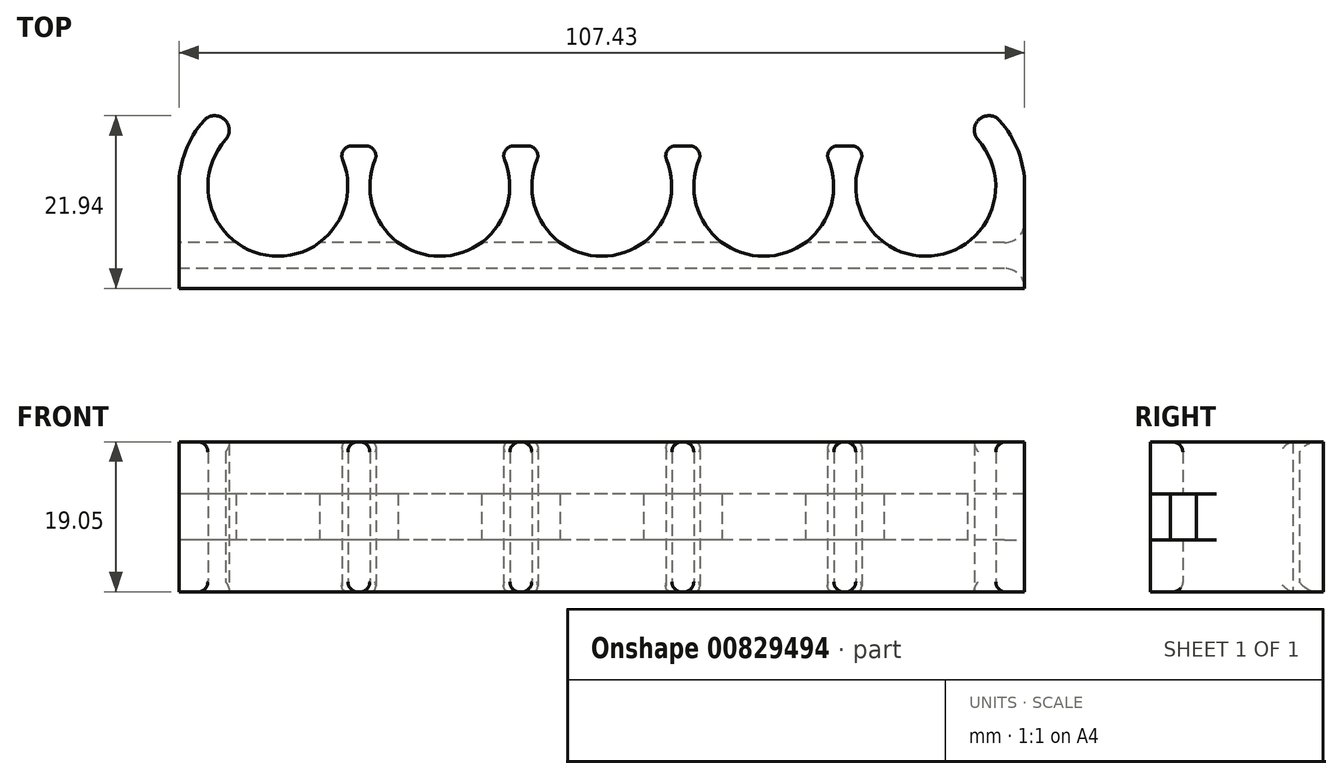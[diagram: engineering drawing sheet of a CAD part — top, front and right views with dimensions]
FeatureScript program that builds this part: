
annotation { "Feature Type Name" : "Feature", "Feature Type Description" : "" }
export const myFeature = defineFeature(function(context is Context, id is Id, definition is map)
    precondition{}
    {
        {
            var Q0;
            Q0=qCreatedBy(makeId("Top.planeOp"),FACE);
            var sketch = newSketch(context, id + "F0", { "sketchPlane" : qUnion([Q0])});
            skLineSegment(sketch, "E0.direction1", {"start": v(0, 0) * mm, "end": v(20.57, 0) * mm, "construction": true});
            skLineSegment(sketch, "E1", {"start": v(9.4, 5.14) * mm, "end": v(11.18, 5.14) * mm});
            skLineSegment(sketch, "E2", {"start": v(29.97, 5.14) * mm, "end": v(31.75, 5.14) * mm});
            skArc(sketch, "E3.MirrorCS", {"start": v(-9.4, 8.35) * mm, "mid": v(-6.78, 8.5) * mm, "end": v(-6.66, 5.9) * mm});
            skArc(sketch, "E4.MirrorCS", {"start": v(-12.57, 0) * mm, "mid": v(-11.75, 4.47) * mm, "end": v(-9.4, 8.35) * mm});
            skLineSegment(sketch, "E5.MirrorCS", {"start": v(-12.57, -12.97) * mm, "end": v(-12.57, 0) * mm});
            skArc(sketch, "E6", {"start": v(8.22, 3.38) * mm, "mid": v(-1.5, -8.76) * mm, "end": v(-6.63, 5.93) * mm});
            skArc(sketch, "E7", {"start": v(28.8, 3.38) * mm, "mid": v(20.57, -8.89) * mm, "end": v(12.35, 3.38) * mm});
            skPoint(sketch, "E8.visualSharp", {"position": v(7.26, 5.14) * mm});
            skArc(sketch, "E8.filletArc", {"start": v(9.4, 5.14) * mm, "mid": v(8.34, 4.57) * mm, "end": v(8.22, 3.38) * mm});
            skPoint(sketch, "E9.visualSharp", {"position": v(13.32, 5.14) * mm});
            skArc(sketch, "E9.filletArc", {"start": v(12.35, 3.38) * mm, "mid": v(12.23, 4.57) * mm, "end": v(11.18, 5.14) * mm});
            skPoint(sketch, "E10.visualSharp", {"position": v(27.83, 5.14) * mm});
            skArc(sketch, "E10.filletArc", {"start": v(29.97, 5.14) * mm, "mid": v(28.91, 4.57) * mm, "end": v(28.8, 3.38) * mm});
            skPoint(sketch, "E11.visualSharp", {"position": v(33.9, 5.14) * mm});
            skArc(sketch, "E11.filletArc", {"start": v(32.93, 3.38) * mm, "mid": v(32.8, 4.57) * mm, "end": v(31.75, 5.14) * mm});
            skLineSegment(sketch, "E12", {"start": v(50.54, 5.14) * mm, "end": v(52.33, 5.14) * mm});
            skArc(sketch, "E13", {"start": v(49.37, 3.38) * mm, "mid": v(41.15, -8.9) * mm, "end": v(32.93, 3.38) * mm});
            skPoint(sketch, "E14.visualSharp", {"position": v(48.4, 5.14) * mm});
            skArc(sketch, "E14.filletArc", {"start": v(50.54, 5.14) * mm, "mid": v(49.49, 4.57) * mm, "end": v(49.37, 3.38) * mm});
            skPoint(sketch, "E15.visualSharp", {"position": v(54.47, 5.14) * mm});
            skArc(sketch, "E15.filletArc", {"start": v(53.5, 3.38) * mm, "mid": v(53.38, 4.57) * mm, "end": v(52.33, 5.14) * mm});
            skLineSegment(sketch, "E16", {"start": v(94.86, -12.97) * mm, "end": v(94.86, 0) * mm});
            skLineSegment(sketch, "E17", {"start": v(71.12, 5.14) * mm, "end": v(72.9, 5.14) * mm});
            skArc(sketch, "E18", {"start": v(94.86, 0) * mm, "mid": v(94.04, 4.47) * mm, "end": v(91.69, 8.35) * mm});
            skArc(sketch, "E19", {"start": v(91.69, 8.35) * mm, "mid": v(89.09, 8.5) * mm, "end": v(88.94, 5.9) * mm});
            skArc(sketch, "E20", {"start": v(69.94, 3.38) * mm, "mid": v(61.72, -8.9) * mm, "end": v(53.5, 3.38) * mm});
            skArc(sketch, "E21", {"start": v(88.94, 5.9) * mm, "mid": v(83.79, -8.76) * mm, "end": v(74.07, 3.38) * mm});
            skPoint(sketch, "E22.visualSharp", {"position": v(68.98, 5.14) * mm});
            skArc(sketch, "E22.filletArc", {"start": v(71.12, 5.14) * mm, "mid": v(70.06, 4.57) * mm, "end": v(69.94, 3.38) * mm});
            skPoint(sketch, "E23.visualSharp", {"position": v(75.04, 5.14) * mm});
            skArc(sketch, "E23.filletArc", {"start": v(74.07, 3.38) * mm, "mid": v(73.96, 4.57) * mm, "end": v(72.9, 5.14) * mm});
            skLineSegment(sketch, "E24", {"start": v(-12.57, -12.97) * mm, "end": v(94.86, -12.97) * mm});
            skSolve(sketch);
        }
        {
            var Q0;
            Q0=makeQuery(id+"F0.imprint","IMPRINT",FACE,{"disambiguationData":[TD([[makeQuery(id+"F0.imprint","IMPRINT",EDGE,{"derivedFrom":sQuery(id+"F0.wireOp",EDGE,"E1")}),-1.0]])]});
            var Q1;
            Q1=sQuery(id+"F0.wireOp",EDGE,"369ZI1eD-I4s6-VPlC-i9KF-M6xCAj87r0oj");
            var Q2;
            Q2=sQuery(id+"F0.wireOp",EDGE,"E6");
            var Q3;
            Q3=sQuery(id+"F0.wireOp",EDGE,"E3.MirrorCS");
            var Q4;
            Q4=sQuery(id+"F0.wireOp",EDGE,"E4.MirrorCS");
            var Q5;
            Q5=sQuery(id+"F0.wireOp",EDGE,"E5.MirrorCS");
            var Q6;
            Q6=sQuery(id+"F0.wireOp",EDGE,"E7");
            var Q7;
            Q7=sQuery(id+"F0.wireOp",EDGE,"E13");
            var Q8;
            Q8=sQuery(id+"F0.wireOp",EDGE,"21338633-60fe-4fad-beaa-767240a8ec89");
            var Q9;
            Q9=sQuery(id+"F0.wireOp",EDGE,"4f3b21b5-788c-469e-a292-998afeaadf8e");
            var Q10;
            Q10=sQuery(id+"F0.wireOp",EDGE,"75842ce1-2111-4564-b153-1218a2f22df0");
            var Q11;
            Q11=sQuery(id+"F0.wireOp",EDGE,"88b2d735-7f10-4ffd-a21d-1716e4e02eba");
            var Q12;
            Q12=sQuery(id+"F0.wireOp",EDGE,"E15.filletArc");
            var Q13;
            Q13=sQuery(id+"F0.wireOp",EDGE,"E12");
            var Q14;
            Q14=sQuery(id+"F0.wireOp",EDGE,"E14.filletArc");
            var Q15;
            Q15=sQuery(id+"F0.wireOp",EDGE,"E11.filletArc");
            var Q16;
            Q16=sQuery(id+"F0.wireOp",EDGE,"E2");
            var Q17;
            Q17=sQuery(id+"F0.wireOp",EDGE,"E10.filletArc");
            var Q18;
            Q18=sQuery(id+"F0.wireOp",EDGE,"E9.filletArc");
            var Q19;
            Q19=sQuery(id+"F0.wireOp",EDGE,"E1");
            var Q20;
            Q20=sQuery(id+"F0.wireOp",EDGE,"E8.filletArc");
            extrude(context, id + "F1", {"entities" : qUnion([Q0]), "surfaceEntities" : qUnion([Q1, Q2, Q3, Q4, Q5, Q6, Q7, Q8, Q9, Q10, Q11, Q12, Q13, Q14, Q15, Q16, Q17, Q18, Q19, Q20]), "depth" : 19.05 * mm, "offsetDistance" : 25.4 * mm});
        }
        {
            var Q0;
            Q0=makeQuery(id+"F1.opExtrude","SWEPT_FACE",FACE,{"disambiguationData":[OSD([sQuery(id+"F0.wireOp",EDGE,"E5.MirrorCS")])]});
            var Q1;
            Q1 = qBodyType(qCreatedBy(id + "F3" ,EDGE), BodyType.WIRE);
            cPlane(context, id + "F2", {"entities" : qUnion([Q0, Q1]), "cplaneType" : CPlaneType.OFFSET, "offset" : 0 * mm, "width" : 152.4 * mm, "height" : 152.4 * mm});
        }
        {
            var Q0;
            Q0=qCreatedBy(id+"F2.planeOp",FACE);
            var sketch = newSketch(context, id + "F3", { "sketchPlane" : qUnion([Q0])});
            skLineSegment(sketch, "E25.bottom", {"start": v(7.13, 12.45) * mm, "end": v(10.43, 12.45) * mm});
            skLineSegment(sketch, "E25.top", {"start": v(7.13, 6.6) * mm, "end": v(10.43, 6.6) * mm});
            skLineSegment(sketch, "E25.left", {"start": v(7.13, 12.45) * mm, "end": v(7.13, 6.6) * mm});
            skLineSegment(sketch, "E25.right", {"start": v(10.43, 12.45) * mm, "end": v(10.43, 6.6) * mm});
            skLineSegment(sketch, "E26", {"start": v(10.43, 9.53) * mm, "end": v(7.13, 9.53) * mm, "construction": true});
            skLineSegment(sketch, "E27", {"start": v(12.97, 9.53) * mm, "end": v(7.13, 9.53) * mm, "construction": true});
            skSolve(sketch);
        }
        {
            var Q0;
            Q0=makeQuery(id+"F3.imprint","IMPRINT",FACE,{"disambiguationData":[TD([[makeQuery(id+"F3.imprint","IMPRINT",EDGE,{"derivedFrom":sQuery(id+"F3.wireOp",EDGE,"E25.bottom")}),-1.0]])]});
            extrude(context, id + "F4", {"entities" : qUnion([Q0]), "operationType" : NewBodyOperationType.REMOVE, "endBound" : BoundingType.THROUGH_ALL, "oppositeDirection" : true, "depth" : 25.4 * mm, "offsetDistance" : 25.4 * mm});
        }
        {
            var Q0;
            Q0=makeQuery(id+"F4.boolean.opBoolean","INTERSECT",EDGE,{"derivedFrom":[makeQuery(id+"F1.opExtrude","SWEPT_FACE",FACE,{"disambiguationData":[OSD([sQuery(id+"F0.wireOp",EDGE,"E16")])]}),makeQuery(id+"F4.opExtrude","SWEPT_FACE",FACE,{"disambiguationData":[OSD([sQuery(id+"F3.wireOp",EDGE,"E25.left")])]})]});
            var Q1;
            Q1=makeQuery(id+"F4.boolean.opBoolean","INTERSECT",EDGE,{"derivedFrom":[makeQuery(id+"F1.opExtrude","SWEPT_FACE",FACE,{"disambiguationData":[OSD([sQuery(id+"F0.wireOp",EDGE,"E16")])]}),makeQuery(id+"F4.opExtrude","SWEPT_FACE",FACE,{"disambiguationData":[OSD([sQuery(id+"F3.wireOp",EDGE,"E25.right")])]})]});
            var Q2;
            Q2=makeQuery(id+"F4.boolean.opBoolean","COPY",EDGE,{"derivedFrom":makeQuery(id+"F4.opExtrude","CAP_EDGE",EDGE,{"disambiguationData":[OSD([sQuery(id+"F3.wireOp",EDGE,"E25.left")])],"isStart":true})});
            var Q3;
            Q3=makeQuery(id+"F4.boolean.opBoolean","COPY",EDGE,{"derivedFrom":makeQuery(id+"F4.opExtrude","CAP_EDGE",EDGE,{"disambiguationData":[OSD([sQuery(id+"F3.wireOp",EDGE,"E25.right")])],"isStart":true})});
            fillet(context, id + "F5", {"entities" : qUnion([Q0, Q1, Q2, Q3]), "radius" : 2.54 * mm, "tangentPropagation" : true, "allowEdgeOverflow" : false});
        }
        {
            var Q0;
            Q0=makeQuery(id+"F1.opExtrude","CAP_EDGE",EDGE,{"disambiguationData":[OSD([sQuery(id+"F0.wireOp",EDGE,"wjlftGJZ-UNCk-L4i5-wpio-xcS1ndEBSDBN")])],"isStart":true});
            var Q1;
            Q1=makeQuery(id+"F1.opExtrude","CAP_EDGE",EDGE,{"disambiguationData":[OSD([sQuery(id+"F0.wireOp",EDGE,"E7")])],"isStart":true});
            var Q2;
            Q2=makeQuery(id+"F1.opExtrude","CAP_EDGE",EDGE,{"disambiguationData":[OSD([sQuery(id+"F0.wireOp",EDGE,"E6")])],"isStart":true});
            var Q3;
            Q3=makeQuery(id+"F1.opExtrude","CAP_EDGE",EDGE,{"disambiguationData":[OSD([sQuery(id+"F0.wireOp",EDGE,"E13")])],"isStart":true});
            var Q4;
            Q4=makeQuery(id+"F1.opExtrude","CAP_EDGE",EDGE,{"disambiguationData":[OSD([sQuery(id+"F0.wireOp",EDGE,"E20")])],"isStart":true});
            var Q5;
            Q5=makeQuery(id+"F1.opExtrude","CAP_EDGE",EDGE,{"disambiguationData":[OSD([sQuery(id+"F0.wireOp",EDGE,"E21")])],"isStart":true});
            var Q6;
            Q6=makeQuery(id+"F1.opExtrude","CAP_EDGE",EDGE,{"disambiguationData":[OSD([sQuery(id+"F0.wireOp",EDGE,"E21")])],"isStart":false});
            var Q7;
            Q7=makeQuery(id+"F1.opExtrude","CAP_EDGE",EDGE,{"disambiguationData":[OSD([sQuery(id+"F0.wireOp",EDGE,"E20")])],"isStart":false});
            var Q8;
            Q8=makeQuery(id+"F1.opExtrude","CAP_EDGE",EDGE,{"disambiguationData":[OSD([sQuery(id+"F0.wireOp",EDGE,"E13")])],"isStart":false});
            var Q9;
            Q9=makeQuery(id+"F1.opExtrude","CAP_EDGE",EDGE,{"disambiguationData":[OSD([sQuery(id+"F0.wireOp",EDGE,"E6")])],"isStart":false});
            var Q10;
            Q10=makeQuery(id+"F1.opExtrude","CAP_EDGE",EDGE,{"disambiguationData":[OSD([sQuery(id+"F0.wireOp",EDGE,"E7")])],"isStart":false});
            fillet(context, id + "F6", {"entities" : qUnion([Q0, Q1, Q2, Q3, Q4, Q5, Q6, Q7, Q8, Q9, Q10]), "radius" : 1.27 * mm, "allowEdgeOverflow" : false});
        }
    });
